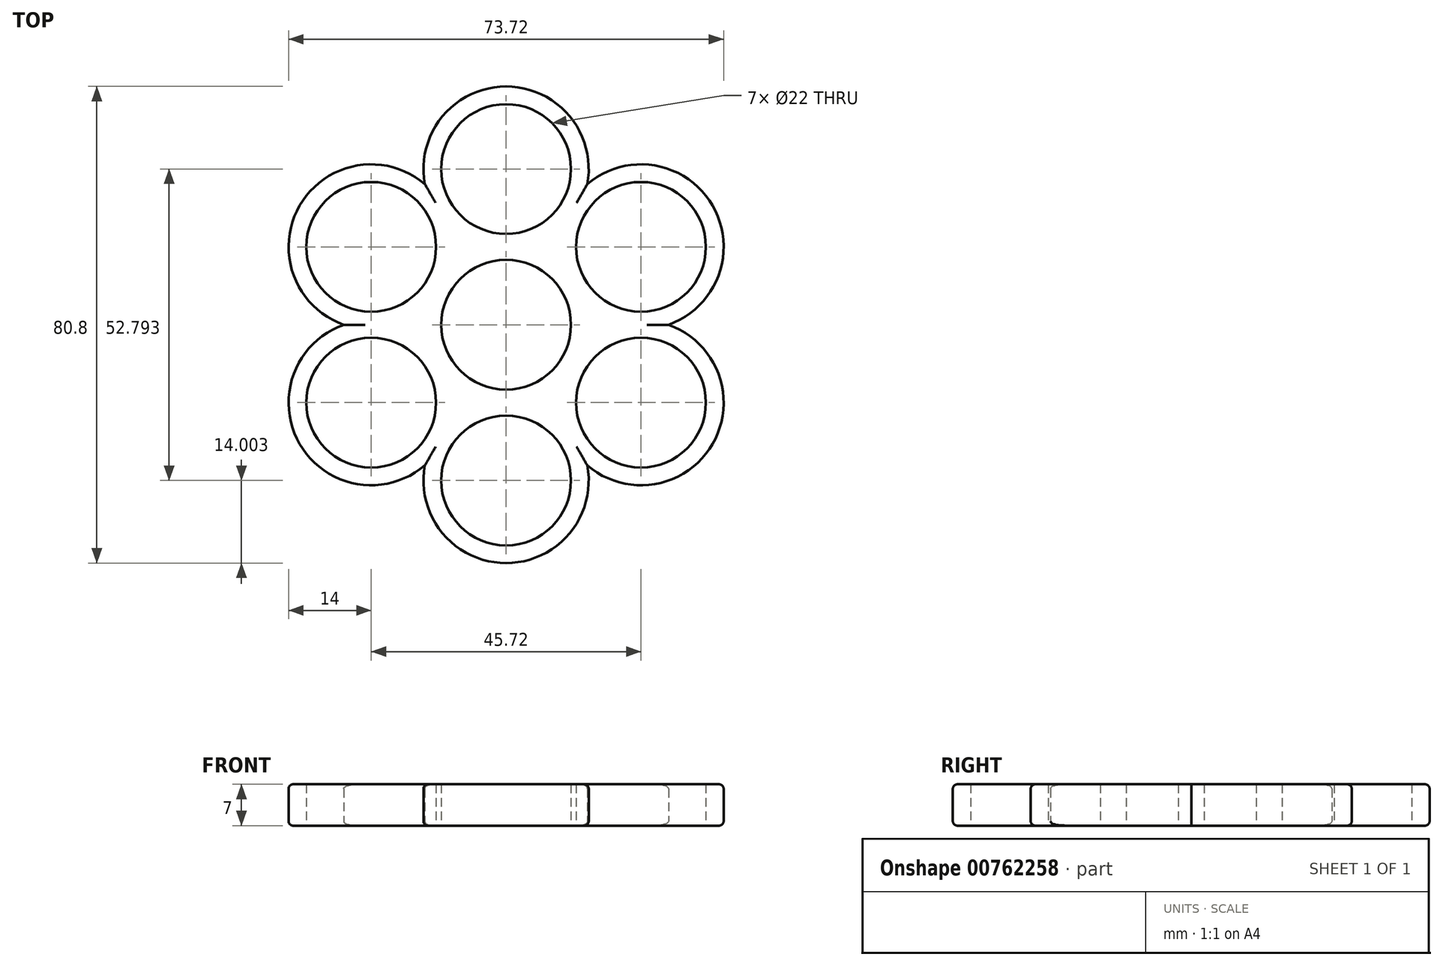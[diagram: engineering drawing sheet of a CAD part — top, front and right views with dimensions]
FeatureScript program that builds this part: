
annotation { "Feature Type Name" : "Feature", "Feature Type Description" : "" }
export const myFeature = defineFeature(function(context is Context, id is Id, definition is map)
    precondition{}
    {
        {
            var Q0;
            Q0=qCreatedBy(makeId("Top.planeOp"),FACE);
            var sketch = newSketch(context, id + "F0", { "sketchPlane" : qUnion([Q0])});
            skCircle(sketch, "E0.cCircle", {"center": v(0, 0) * mm, "radius": 22.86 * mm, "construction": true});
            skLineSegment(sketch, "E0.0", {"start": v(22.86, 13.2) * mm, "end": v(22.86, -13.2) * mm});
            skLineSegment(sketch, "E0.1", {"start": v(22.86, -13.2) * mm, "end": v(0, -26.4) * mm});
            skLineSegment(sketch, "E0.2", {"start": v(0, -26.4) * mm, "end": v(-22.86, -13.2) * mm});
            skLineSegment(sketch, "E0.3", {"start": v(-22.86, -13.2) * mm, "end": v(-22.86, 13.2) * mm});
            skLineSegment(sketch, "E0.4", {"start": v(-22.86, 13.2) * mm, "end": v(0, 26.4) * mm});
            skLineSegment(sketch, "E0.5", {"start": v(0, 26.4) * mm, "end": v(22.86, 13.2) * mm});
            skPoint(sketch, "E0.0.midPoint", {"position": v(22.86, 0) * mm});
            skCircle(sketch, "E1", {"center": v(0, 26.4) * mm, "radius": 11 * mm});
            skCircle(sketch, "E2", {"center": v(-22.86, 13.2) * mm, "radius": 11 * mm});
            skCircle(sketch, "E3", {"center": v(-22.86, -13.2) * mm, "radius": 11 * mm});
            skCircle(sketch, "E4", {"center": v(0, -26.4) * mm, "radius": 11 * mm});
            skCircle(sketch, "E5", {"center": v(22.86, -13.2) * mm, "radius": 11 * mm});
            skCircle(sketch, "E6", {"center": v(22.86, 13.2) * mm, "radius": 11 * mm});
            skCircle(sketch, "E7", {"center": v(-22.86, -13.2) * mm, "radius": 14 * mm});
            skCircle(sketch, "E8", {"center": v(-22.86, 13.2) * mm, "radius": 14 * mm});
            skCircle(sketch, "E9", {"center": v(0, 26.4) * mm, "radius": 14 * mm});
            skCircle(sketch, "E10", {"center": v(22.86, 13.2) * mm, "radius": 14 * mm});
            skCircle(sketch, "E11", {"center": v(22.86, -13.2) * mm, "radius": 14 * mm});
            skCircle(sketch, "E12", {"center": v(0, -26.4) * mm, "radius": 14 * mm});
            skCircle(sketch, "E13", {"center": v(0, 0) * mm, "radius": 11 * mm});
            skSolve(sketch);
        }
        {
            var Q0;
            Q0=makeQuery(id+"F0.imprint","IMPRINT",FACE,{"disambiguationData":[TD([[makeQuery(id+"F0.imprint","IMPRINT",EDGE,{"derivedFrom":sQuery(id+"F0.wireOp",EDGE,"E13")}),-1.0]])]});
            var Q1;
            {var subQ6=sQuery(id+"F0.wireOp",EDGE,"E0.1");var subQ9=sQuery(id+"F0.wireOp",EDGE,"E11");var subQ11=makeQuery(id+"F0.imprint","INTERSECT",VERTEX,{"derivedFrom":[subQ6,subQ9]});Q1=makeQuery(id+"F0.imprint","IMPRINT",FACE,{"disambiguationData":[TD([[makeQuery(id+"F0.imprint","IMPRINT",EDGE,{"disambiguationData":[TD([[subQ11,-1.0]])],"derivedFrom":subQ6}),1.0]])]});}
            var Q2;
            {var subQ6=sQuery(id+"F0.wireOp",EDGE,"E0.1");var subQ9=sQuery(id+"F0.wireOp",EDGE,"E11");var subQ10=makeQuery(id+"F0.imprint","INTERSECT",VERTEX,{"derivedFrom":[subQ6,subQ9]});Q2=makeQuery(id+"F0.imprint","IMPRINT",FACE,{"disambiguationData":[TD([[makeQuery(id+"F0.imprint","IMPRINT",EDGE,{"disambiguationData":[TD([[subQ10,-1.0]])],"derivedFrom":subQ6}),-1.0]])]});}
            var Q3;
            {var subQ0=sQuery(id+"F0.wireOp",EDGE,"E12");var subQ1=sQuery(id+"F0.wireOp",EDGE,"E0.1");var subQ2=makeQuery(id+"F0.imprint","INTERSECT",VERTEX,{"derivedFrom":[subQ1,subQ0]});Q3=makeQuery(id+"F0.imprint","IMPRINT",FACE,{"disambiguationData":[TD([[makeQuery(id+"F0.imprint","IMPRINT",EDGE,{"disambiguationData":[TD([[subQ2,-1.0]])],"derivedFrom":subQ1}),1.0]])]});}
            var Q4;
            {var subQ1=sQuery(id+"F0.wireOp",EDGE,"E10");var subQ3=sQuery(id+"F0.wireOp",EDGE,"E0.0");var subQ4=makeQuery(id+"F0.imprint","INTERSECT",VERTEX,{"derivedFrom":[subQ3,subQ1]});Q4=makeQuery(id+"F0.imprint","IMPRINT",FACE,{"disambiguationData":[TD([[makeQuery(id+"F0.imprint","IMPRINT",EDGE,{"disambiguationData":[TD([[subQ4,-1.0]])],"derivedFrom":subQ3}),1.0]])]});}
            var Q5;
            {var subQ0=sQuery(id+"F0.wireOp",EDGE,"E12");var subQ1=sQuery(id+"F0.wireOp",EDGE,"E0.1");var subQ2=makeQuery(id+"F0.imprint","INTERSECT",VERTEX,{"derivedFrom":[subQ1,subQ0]});Q5=makeQuery(id+"F0.imprint","IMPRINT",FACE,{"disambiguationData":[TD([[makeQuery(id+"F0.imprint","IMPRINT",EDGE,{"disambiguationData":[TD([[subQ2,-1.0]])],"derivedFrom":subQ1}),-1.0]])]});}
            var Q6;
            {var subQ5=sQuery(id+"F0.wireOp",EDGE,"E10");var subQ6=sQuery(id+"F0.wireOp",EDGE,"E0.0");var subQ7=makeQuery(id+"F0.imprint","INTERSECT",VERTEX,{"derivedFrom":[subQ6,subQ5]});Q6=makeQuery(id+"F0.imprint","IMPRINT",FACE,{"disambiguationData":[TD([[makeQuery(id+"F0.imprint","IMPRINT",EDGE,{"disambiguationData":[TD([[subQ7,-1.0]])],"derivedFrom":subQ6}),-1.0]])]});}
            var Q7;
            {var subQ5=sQuery(id+"F0.wireOp",EDGE,"E6");var subQ7=sQuery(id+"F0.wireOp",EDGE,"E0.0");var subQ8=makeQuery(id+"F0.imprint","INTERSECT",VERTEX,{"derivedFrom":[subQ7,subQ5]});Q7=makeQuery(id+"F0.imprint","IMPRINT",FACE,{"disambiguationData":[TD([[makeQuery(id+"F0.imprint","IMPRINT",EDGE,{"disambiguationData":[TD([[subQ8,-1.0]])],"derivedFrom":subQ7}),1.0]])]});}
            var Q8;
            {var subQ5=sQuery(id+"F0.wireOp",EDGE,"E6");var subQ6=sQuery(id+"F0.wireOp",EDGE,"E0.0");var subQ7=makeQuery(id+"F0.imprint","INTERSECT",VERTEX,{"derivedFrom":[subQ6,subQ5]});Q8=makeQuery(id+"F0.imprint","IMPRINT",FACE,{"disambiguationData":[TD([[makeQuery(id+"F0.imprint","IMPRINT",EDGE,{"disambiguationData":[TD([[subQ7,-1.0]])],"derivedFrom":subQ6}),-1.0]])]});}
            var Q9;
            {var subQ0=sQuery(id+"F0.wireOp",EDGE,"E11");var subQ1=sQuery(id+"F0.wireOp",EDGE,"E0.0");var subQ2=makeQuery(id+"F0.imprint","INTERSECT",VERTEX,{"derivedFrom":[subQ1,subQ0]});Q9=makeQuery(id+"F0.imprint","IMPRINT",FACE,{"disambiguationData":[TD([[makeQuery(id+"F0.imprint","IMPRINT",EDGE,{"disambiguationData":[TD([[subQ2,-1.0]])],"derivedFrom":subQ1}),1.0]])]});}
            var Q10;
            {var subQ0=sQuery(id+"F0.wireOp",EDGE,"E11");var subQ1=sQuery(id+"F0.wireOp",EDGE,"E0.0");var subQ2=makeQuery(id+"F0.imprint","INTERSECT",VERTEX,{"derivedFrom":[subQ1,subQ0]});Q10=makeQuery(id+"F0.imprint","IMPRINT",FACE,{"disambiguationData":[TD([[makeQuery(id+"F0.imprint","IMPRINT",EDGE,{"disambiguationData":[TD([[subQ2,-1.0]])],"derivedFrom":subQ1}),-1.0]])]});}
            var Q11;
            {var subQ1=sQuery(id+"F0.wireOp",EDGE,"E0.4");var subQ7=sQuery(id+"F0.wireOp",EDGE,"E8");var subQ8=makeQuery(id+"F0.imprint","INTERSECT",VERTEX,{"derivedFrom":[subQ1,subQ7]});Q11=makeQuery(id+"F0.imprint","IMPRINT",FACE,{"disambiguationData":[TD([[makeQuery(id+"F0.imprint","IMPRINT",EDGE,{"disambiguationData":[TD([[subQ8,-1.0]])],"derivedFrom":subQ1}),-1.0]])]});}
            var Q12;
            {var subQ1=sQuery(id+"F0.wireOp",EDGE,"E8");var subQ3=sQuery(id+"F0.wireOp",EDGE,"E0.4");var subQ4=makeQuery(id+"F0.imprint","INTERSECT",VERTEX,{"derivedFrom":[subQ3,subQ1]});Q12=makeQuery(id+"F0.imprint","IMPRINT",FACE,{"disambiguationData":[TD([[makeQuery(id+"F0.imprint","IMPRINT",EDGE,{"disambiguationData":[TD([[subQ4,-1.0]])],"derivedFrom":subQ3}),1.0]])]});}
            var Q13;
            {var subQ0=sQuery(id+"F0.wireOp",EDGE,"E10");var subQ1=sQuery(id+"F0.wireOp",EDGE,"E0.5");var subQ2=makeQuery(id+"F0.imprint","INTERSECT",VERTEX,{"derivedFrom":[subQ1,subQ0]});Q13=makeQuery(id+"F0.imprint","IMPRINT",FACE,{"disambiguationData":[TD([[makeQuery(id+"F0.imprint","IMPRINT",EDGE,{"disambiguationData":[TD([[subQ2,-1.0]])],"derivedFrom":subQ1}),1.0]])]});}
            var Q14;
            {var subQ0=sQuery(id+"F0.wireOp",EDGE,"E10");var subQ1=sQuery(id+"F0.wireOp",EDGE,"E0.5");var subQ2=makeQuery(id+"F0.imprint","INTERSECT",VERTEX,{"derivedFrom":[subQ1,subQ0]});Q14=makeQuery(id+"F0.imprint","IMPRINT",FACE,{"disambiguationData":[TD([[makeQuery(id+"F0.imprint","IMPRINT",EDGE,{"disambiguationData":[TD([[subQ2,-1.0]])],"derivedFrom":subQ1}),-1.0]])]});}
            var Q15;
            {var subQ0=sQuery(id+"F0.wireOp",EDGE,"E9");var subQ1=sQuery(id+"F0.wireOp",EDGE,"E0.4");var subQ2=makeQuery(id+"F0.imprint","INTERSECT",VERTEX,{"derivedFrom":[subQ1,subQ0]});Q15=makeQuery(id+"F0.imprint","IMPRINT",FACE,{"disambiguationData":[TD([[makeQuery(id+"F0.imprint","IMPRINT",EDGE,{"disambiguationData":[TD([[subQ2,-1.0]])],"derivedFrom":subQ1}),-1.0]])]});}
            var Q16;
            {var subQ0=sQuery(id+"F0.wireOp",EDGE,"E9");var subQ1=sQuery(id+"F0.wireOp",EDGE,"E0.4");var subQ2=makeQuery(id+"F0.imprint","INTERSECT",VERTEX,{"derivedFrom":[subQ1,subQ0]});Q16=makeQuery(id+"F0.imprint","IMPRINT",FACE,{"disambiguationData":[TD([[makeQuery(id+"F0.imprint","IMPRINT",EDGE,{"disambiguationData":[TD([[subQ2,-1.0]])],"derivedFrom":subQ1}),1.0]])]});}
            var Q17;
            {var subQ1=sQuery(id+"F0.wireOp",EDGE,"E0.3");var subQ8=sQuery(id+"F0.wireOp",EDGE,"E7");var subQ10=makeQuery(id+"F0.imprint","INTERSECT",VERTEX,{"derivedFrom":[subQ1,subQ8]});Q17=makeQuery(id+"F0.imprint","IMPRINT",FACE,{"disambiguationData":[TD([[makeQuery(id+"F0.imprint","IMPRINT",EDGE,{"disambiguationData":[TD([[subQ10,-1.0]])],"derivedFrom":subQ1}),1.0]])]});}
            var Q18;
            {var subQ0=sQuery(id+"F0.wireOp",EDGE,"E7");var subQ1=sQuery(id+"F0.wireOp",EDGE,"E0.3");var subQ2=makeQuery(id+"F0.imprint","INTERSECT",VERTEX,{"derivedFrom":[subQ1,subQ0]});Q18=makeQuery(id+"F0.imprint","IMPRINT",FACE,{"disambiguationData":[TD([[makeQuery(id+"F0.imprint","IMPRINT",EDGE,{"disambiguationData":[TD([[subQ2,-1.0]])],"derivedFrom":subQ1}),-1.0]])]});}
            var Q19;
            {var subQ3=sQuery(id+"F0.wireOp",EDGE,"E12");var subQ6=sQuery(id+"F0.wireOp",EDGE,"E0.2");var subQ11=makeQuery(id+"F0.imprint","INTERSECT",VERTEX,{"derivedFrom":[subQ6,subQ3]});Q19=makeQuery(id+"F0.imprint","IMPRINT",FACE,{"disambiguationData":[TD([[makeQuery(id+"F0.imprint","IMPRINT",EDGE,{"disambiguationData":[TD([[subQ11,-1.0]])],"derivedFrom":subQ6}),1.0]])]});}
            var Q20;
            {var subQ3=sQuery(id+"F0.wireOp",EDGE,"E12");var subQ6=sQuery(id+"F0.wireOp",EDGE,"E0.2");var subQ10=makeQuery(id+"F0.imprint","INTERSECT",VERTEX,{"derivedFrom":[subQ6,subQ3]});Q20=makeQuery(id+"F0.imprint","IMPRINT",FACE,{"disambiguationData":[TD([[makeQuery(id+"F0.imprint","IMPRINT",EDGE,{"disambiguationData":[TD([[subQ10,-1.0]])],"derivedFrom":subQ6}),-1.0]])]});}
            var Q21;
            {var subQ0=sQuery(id+"F0.wireOp",EDGE,"E7");var subQ1=sQuery(id+"F0.wireOp",EDGE,"E0.2");var subQ2=makeQuery(id+"F0.imprint","INTERSECT",VERTEX,{"derivedFrom":[subQ1,subQ0]});Q21=makeQuery(id+"F0.imprint","IMPRINT",FACE,{"disambiguationData":[TD([[makeQuery(id+"F0.imprint","IMPRINT",EDGE,{"disambiguationData":[TD([[subQ2,-1.0]])],"derivedFrom":subQ1}),1.0]])]});}
            var Q22;
            {var subQ0=sQuery(id+"F0.wireOp",EDGE,"E7");var subQ1=sQuery(id+"F0.wireOp",EDGE,"E0.2");var subQ2=makeQuery(id+"F0.imprint","INTERSECT",VERTEX,{"derivedFrom":[subQ1,subQ0]});Q22=makeQuery(id+"F0.imprint","IMPRINT",FACE,{"disambiguationData":[TD([[makeQuery(id+"F0.imprint","IMPRINT",EDGE,{"disambiguationData":[TD([[subQ2,-1.0]])],"derivedFrom":subQ1}),-1.0]])]});}
            var Q23;
            {var subQ0=sQuery(id+"F0.wireOp",EDGE,"E8");var subQ1=sQuery(id+"F0.wireOp",EDGE,"E0.3");var subQ2=makeQuery(id+"F0.imprint","INTERSECT",VERTEX,{"derivedFrom":[subQ1,subQ0]});Q23=makeQuery(id+"F0.imprint","IMPRINT",FACE,{"disambiguationData":[TD([[makeQuery(id+"F0.imprint","IMPRINT",EDGE,{"disambiguationData":[TD([[subQ2,-1.0]])],"derivedFrom":subQ1}),-1.0]])]});}
            var Q24;
            {var subQ0=sQuery(id+"F0.wireOp",EDGE,"E8");var subQ1=sQuery(id+"F0.wireOp",EDGE,"E0.3");var subQ2=makeQuery(id+"F0.imprint","INTERSECT",VERTEX,{"derivedFrom":[subQ1,subQ0]});Q24=makeQuery(id+"F0.imprint","IMPRINT",FACE,{"disambiguationData":[TD([[makeQuery(id+"F0.imprint","IMPRINT",EDGE,{"disambiguationData":[TD([[subQ2,-1.0]])],"derivedFrom":subQ1}),1.0]])]});}
            extrude(context, id + "F1", {"entities" : qUnion([Q0, Q1, Q2, Q3, Q4, Q5, Q6, Q7, Q8, Q9, Q10, Q11, Q12, Q13, Q14, Q15, Q16, Q17, Q18, Q19, Q20, Q21, Q22, Q23, Q24]), "depth" : 7 * mm, "offsetDistance" : 25.4 * mm});
        }
        {
            var Q0;
            Q0=makeQuery(id+"F1.opExtrude","CAP_EDGE",EDGE,{"disambiguationData":[OSD([sQuery(id+"F0.wireOp",EDGE,"E8")])],"isStart":false});
            var Q1;
            Q1=makeQuery(id+"F1.opExtrude","CAP_EDGE",EDGE,{"disambiguationData":[OSD([sQuery(id+"F0.wireOp",EDGE,"E9")])],"isStart":false});
            var Q2;
            Q2=makeQuery(id+"F1.opExtrude","CAP_EDGE",EDGE,{"disambiguationData":[OSD([sQuery(id+"F0.wireOp",EDGE,"E10")])],"isStart":false});
            var Q3;
            Q3=makeQuery(id+"F1.opExtrude","CAP_EDGE",EDGE,{"disambiguationData":[OSD([sQuery(id+"F0.wireOp",EDGE,"E11")])],"isStart":false});
            var Q4;
            Q4=makeQuery(id+"F1.opExtrude","CAP_EDGE",EDGE,{"disambiguationData":[OSD([sQuery(id+"F0.wireOp",EDGE,"E12")])],"isStart":false});
            var Q5;
            Q5=makeQuery(id+"F1.opExtrude","CAP_EDGE",EDGE,{"disambiguationData":[OSD([sQuery(id+"F0.wireOp",EDGE,"E7")])],"isStart":false});
            var Q6;
            Q6=makeQuery(id+"F1.opExtrude","CAP_EDGE",EDGE,{"disambiguationData":[OSD([sQuery(id+"F0.wireOp",EDGE,"E12")])],"isStart":true});
            var Q7;
            Q7=makeQuery(id+"F1.opExtrude","CAP_EDGE",EDGE,{"disambiguationData":[OSD([sQuery(id+"F0.wireOp",EDGE,"E11")])],"isStart":true});
            var Q8;
            Q8=makeQuery(id+"F1.opExtrude","CAP_EDGE",EDGE,{"disambiguationData":[OSD([sQuery(id+"F0.wireOp",EDGE,"E7")])],"isStart":true});
            var Q9;
            Q9=makeQuery(id+"F1.opExtrude","CAP_EDGE",EDGE,{"disambiguationData":[OSD([sQuery(id+"F0.wireOp",EDGE,"E8")])],"isStart":true});
            var Q10;
            Q10=makeQuery(id+"F1.opExtrude","CAP_EDGE",EDGE,{"disambiguationData":[OSD([sQuery(id+"F0.wireOp",EDGE,"E9")])],"isStart":true});
            var Q11;
            Q11=makeQuery(id+"F1.opExtrude","CAP_EDGE",EDGE,{"disambiguationData":[OSD([sQuery(id+"F0.wireOp",EDGE,"E10")])],"isStart":true});
            fillet(context, id + "F2", {"entities" : qUnion([Q0, Q1, Q2, Q3, Q4, Q5, Q6, Q7, Q8, Q9, Q10, Q11]), "radius" : 0.76 * mm, "tangentPropagation" : true, "allowEdgeOverflow" : false});
        }
    });
